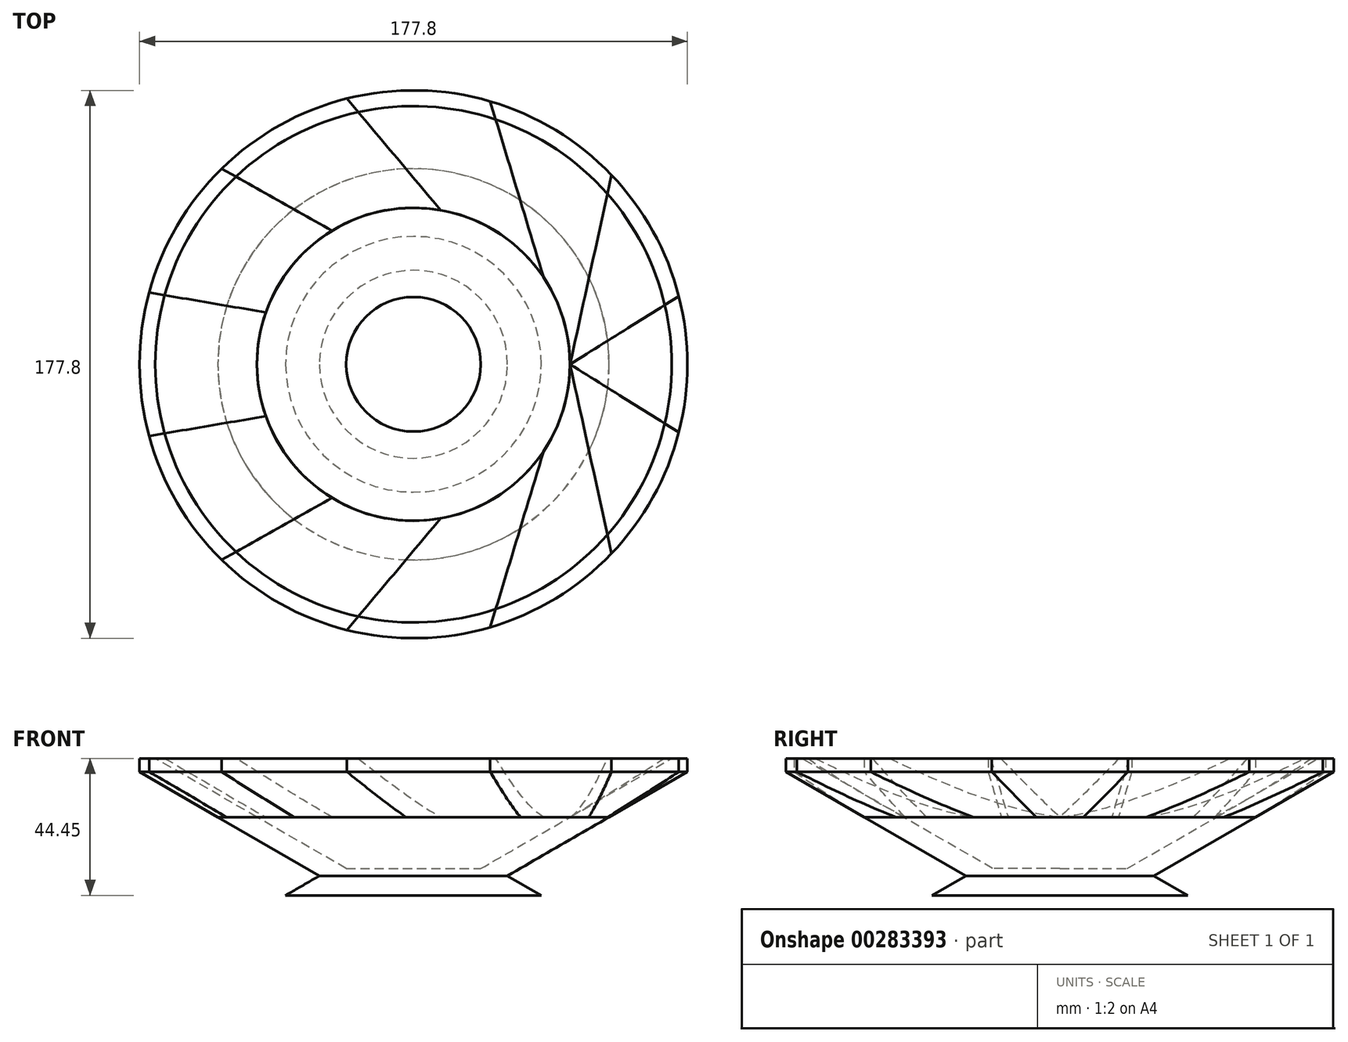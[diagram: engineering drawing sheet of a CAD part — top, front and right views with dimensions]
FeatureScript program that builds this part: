
annotation { "Feature Type Name" : "Feature", "Feature Type Description" : "" }
export const myFeature = defineFeature(function(context is Context, id is Id, definition is map)
    precondition{}
    {
        {
            var Q0;
            Q0=qCreatedBy(makeId("Top.planeOp"),FACE);
            var sketch = newSketch(context, id + "F0", { "sketchPlane" : qUnion([Q0])});
            skCircle(sketch, "E0", {"center": v(0, 0) * mm, "radius": 63.5 * mm});
            skLineSegment(sketch, "E1", {"start": v(0, 0) * mm, "end": v(88.9, 0) * mm, "construction": true});
            skCircle(sketch, "E2.cCircle", {"center": v(0, 0) * mm, "radius": 88.9 * mm});
            skLineSegment(sketch, "E2.0", {"start": v(88.9, 23.82) * mm, "end": v(88.9, -23.82) * mm});
            skLineSegment(sketch, "E2.1", {"start": v(88.9, -23.82) * mm, "end": v(65.08, -65.08) * mm});
            skLineSegment(sketch, "E2.2", {"start": v(65.08, -65.08) * mm, "end": v(23.82, -88.9) * mm});
            skLineSegment(sketch, "E2.3", {"start": v(23.82, -88.9) * mm, "end": v(-23.82, -88.9) * mm});
            skLineSegment(sketch, "E2.4", {"start": v(-23.82, -88.9) * mm, "end": v(-65.08, -65.08) * mm});
            skLineSegment(sketch, "E2.5", {"start": v(-65.08, -65.08) * mm, "end": v(-88.9, -23.82) * mm});
            skLineSegment(sketch, "E2.6", {"start": v(-88.9, -23.82) * mm, "end": v(-88.9, 23.82) * mm});
            skLineSegment(sketch, "E2.7", {"start": v(-88.9, 23.82) * mm, "end": v(-65.08, 65.08) * mm});
            skLineSegment(sketch, "E2.8", {"start": v(-65.08, 65.08) * mm, "end": v(-23.82, 88.9) * mm});
            skLineSegment(sketch, "E2.9", {"start": v(-23.82, 88.9) * mm, "end": v(23.82, 88.9) * mm});
            skLineSegment(sketch, "E2.10", {"start": v(23.82, 88.9) * mm, "end": v(65.08, 65.08) * mm});
            skLineSegment(sketch, "E2.11", {"start": v(65.08, 65.08) * mm, "end": v(88.9, 23.82) * mm});
            skPoint(sketch, "E2.0.midPoint", {"position": v(88.9, 0) * mm});
            skCircle(sketch, "E3", {"center": v(0, 0) * mm, "radius": 50.8 * mm});
            skLineSegment(sketch, "E4", {"start": v(50.8, 0) * mm, "end": v(-65.08, 65.08) * mm, "construction": true});
            skLineSegment(sketch, "E5", {"start": v(50.8, 0) * mm, "end": v(-23.82, 88.9) * mm, "construction": true});
            skLineSegment(sketch, "E6", {"start": v(50.8, 0) * mm, "end": v(23.82, 88.9) * mm, "construction": true});
            skLineSegment(sketch, "E7", {"start": v(50.8, 0) * mm, "end": v(65.08, 65.08) * mm, "construction": true});
            skLineSegment(sketch, "E8", {"start": v(50.8, 0) * mm, "end": v(88.9, 23.82) * mm, "construction": true});
            skLineSegment(sketch, "E9", {"start": v(50.8, 0) * mm, "end": v(88.9, -23.82) * mm, "construction": true});
            skLineSegment(sketch, "E10", {"start": v(50.8, 0) * mm, "end": v(65.08, -65.08) * mm, "construction": true});
            skLineSegment(sketch, "E11", {"start": v(50.8, 0) * mm, "end": v(23.82, -88.9) * mm, "construction": true});
            skLineSegment(sketch, "E12", {"start": v(50.8, 0) * mm, "end": v(-23.82, -88.9) * mm, "construction": true});
            skLineSegment(sketch, "E13", {"start": v(50.8, 0) * mm, "end": v(-65.08, -65.08) * mm, "construction": true});
            skLineSegment(sketch, "E14", {"start": v(-88.9, -23.82) * mm, "end": v(50.8, 0) * mm, "construction": true});
            skLineSegment(sketch, "E15", {"start": v(-88.9, 23.82) * mm, "end": v(50.8, 0) * mm, "construction": true});
            skLineSegment(sketch, "E16", {"start": v(-26.44, -43.38) * mm, "end": v(-65.08, -65.08) * mm});
            skLineSegment(sketch, "E17", {"start": v(-26.44, -43.38) * mm, "end": v(-47.93, -16.83) * mm});
            skLineSegment(sketch, "E18", {"start": v(-88.9, -23.82) * mm, "end": v(-47.93, -16.83) * mm});
            skLineSegment(sketch, "E19", {"start": v(-47.93, -16.83) * mm, "end": v(-47.93, 16.83) * mm});
            skLineSegment(sketch, "E20", {"start": v(-88.9, 23.82) * mm, "end": v(-47.93, 16.83) * mm});
            skLineSegment(sketch, "E21", {"start": v(-26.44, 43.38) * mm, "end": v(-47.93, 16.83) * mm});
            skLineSegment(sketch, "E22", {"start": v(-26.44, 43.38) * mm, "end": v(-65.08, 65.08) * mm});
            skLineSegment(sketch, "E23", {"start": v(-26.44, 43.38) * mm, "end": v(8.8, 50.03) * mm});
            skLineSegment(sketch, "E24", {"start": v(-23.82, 88.9) * mm, "end": v(8.8, 50.03) * mm});
            skLineSegment(sketch, "E25", {"start": v(42.23, 28.23) * mm, "end": v(8.8, 50.03) * mm});
            skLineSegment(sketch, "E26", {"start": v(42.23, 28.23) * mm, "end": v(23.82, 88.9) * mm});
            skLineSegment(sketch, "E27", {"start": v(42.23, 28.23) * mm, "end": v(50.8, 0) * mm});
            skLineSegment(sketch, "E28", {"start": v(50.8, 0) * mm, "end": v(65.08, 65.08) * mm});
            skLineSegment(sketch, "E29", {"start": v(88.9, 23.82) * mm, "end": v(50.8, 0) * mm});
            skLineSegment(sketch, "E30", {"start": v(88.9, -23.82) * mm, "end": v(50.8, 0) * mm});
            skLineSegment(sketch, "E31", {"start": v(65.08, -65.08) * mm, "end": v(50.8, 0) * mm});
            skLineSegment(sketch, "E32", {"start": v(23.82, -88.9) * mm, "end": v(50.8, 0) * mm});
            skLineSegment(sketch, "E33", {"start": v(-23.82, -88.9) * mm, "end": v(8.8, -50.03) * mm});
            skLineSegment(sketch, "E34", {"start": v(8.8, -50.03) * mm, "end": v(-26.44, -43.38) * mm});
            skLineSegment(sketch, "E35", {"start": v(8.8, -50.03) * mm, "end": v(42.23, -28.23) * mm});
            skSolve(sketch);
        }
        {
            var Q0;
            Q0=makeQuery(id+"F0.imprint","IMPRINT",FACE,{"disambiguationData":[TD([[makeQuery(id+"F0.imprint","IMPRINT",EDGE,{"derivedFrom":sQuery(id+"F0.wireOp",EDGE,"E17")}),-1.0]])]});
            var Q1;
            {var subQ0=sQuery(id+"F0.wireOp",EDGE,"E35");Q1=makeQuery(id+"F0.imprint","IMPRINT",FACE,{"disambiguationData":[TD([[makeQuery(id+"F0.imprint","IMPRINT",EDGE,{"derivedFrom":subQ0}),-1.0]])]});}
            var Q2;
            {var subQ0=sQuery(id+"F0.wireOp",EDGE,"E34");Q2=makeQuery(id+"F0.imprint","IMPRINT",FACE,{"disambiguationData":[TD([[makeQuery(id+"F0.imprint","IMPRINT",EDGE,{"derivedFrom":subQ0}),1.0]])]});}
            var Q3;
            {var subQ0=sQuery(id+"F0.wireOp",EDGE,"E17");Q3=makeQuery(id+"F0.imprint","IMPRINT",FACE,{"disambiguationData":[TD([[makeQuery(id+"F0.imprint","IMPRINT",EDGE,{"derivedFrom":subQ0}),1.0]])]});}
            var Q4;
            {var subQ0=sQuery(id+"F0.wireOp",EDGE,"E19");Q4=makeQuery(id+"F0.imprint","IMPRINT",FACE,{"disambiguationData":[TD([[makeQuery(id+"F0.imprint","IMPRINT",EDGE,{"derivedFrom":subQ0}),1.0]])]});}
            var Q5;
            {var subQ0=sQuery(id+"F0.wireOp",EDGE,"E21");Q5=makeQuery(id+"F0.imprint","IMPRINT",FACE,{"disambiguationData":[TD([[makeQuery(id+"F0.imprint","IMPRINT",EDGE,{"derivedFrom":subQ0}),-1.0]])]});}
            var Q6;
            {var subQ0=sQuery(id+"F0.wireOp",EDGE,"E23");Q6=makeQuery(id+"F0.imprint","IMPRINT",FACE,{"disambiguationData":[TD([[makeQuery(id+"F0.imprint","IMPRINT",EDGE,{"derivedFrom":subQ0}),1.0]])]});}
            var Q7;
            {var subQ0=sQuery(id+"F0.wireOp",EDGE,"E24");var subQ1=sQuery(id+"F0.wireOp",EDGE,"E0");var subQ2=makeQuery(id+"F0.imprint","INTERSECT",VERTEX,{"derivedFrom":[subQ1,subQ0]});Q7=makeQuery(id+"F0.imprint","IMPRINT",FACE,{"disambiguationData":[TD([[makeQuery(id+"F0.imprint","IMPRINT",EDGE,{"disambiguationData":[TD([[subQ2,-1.0]])],"derivedFrom":subQ1}),1.0]])]});}
            var Q8;
            {var subQ0=sQuery(id+"F0.wireOp",EDGE,"E22");var subQ1=sQuery(id+"F0.wireOp",EDGE,"E0");var subQ2=makeQuery(id+"F0.imprint","INTERSECT",VERTEX,{"derivedFrom":[subQ1,subQ0]});Q8=makeQuery(id+"F0.imprint","IMPRINT",FACE,{"disambiguationData":[TD([[makeQuery(id+"F0.imprint","IMPRINT",EDGE,{"disambiguationData":[TD([[subQ2,-1.0]])],"derivedFrom":subQ1}),1.0]])]});}
            var Q9;
            {var subQ0=sQuery(id+"F0.wireOp",EDGE,"E20");var subQ1=sQuery(id+"F0.wireOp",EDGE,"E0");var subQ2=makeQuery(id+"F0.imprint","INTERSECT",VERTEX,{"derivedFrom":[subQ1,subQ0]});Q9=makeQuery(id+"F0.imprint","IMPRINT",FACE,{"disambiguationData":[TD([[makeQuery(id+"F0.imprint","IMPRINT",EDGE,{"disambiguationData":[TD([[subQ2,-1.0]])],"derivedFrom":subQ1}),1.0]])]});}
            var Q10;
            {var subQ0=sQuery(id+"F0.wireOp",EDGE,"E18");var subQ1=sQuery(id+"F0.wireOp",EDGE,"E0");var subQ2=makeQuery(id+"F0.imprint","INTERSECT",VERTEX,{"derivedFrom":[subQ1,subQ0]});Q10=makeQuery(id+"F0.imprint","IMPRINT",FACE,{"disambiguationData":[TD([[makeQuery(id+"F0.imprint","IMPRINT",EDGE,{"disambiguationData":[TD([[subQ2,-1.0]])],"derivedFrom":subQ1}),1.0]])]});}
            var Q11;
            {var subQ0=sQuery(id+"F0.wireOp",EDGE,"E16");var subQ1=sQuery(id+"F0.wireOp",EDGE,"E0");var subQ2=makeQuery(id+"F0.imprint","INTERSECT",VERTEX,{"derivedFrom":[subQ1,subQ0]});Q11=makeQuery(id+"F0.imprint","IMPRINT",FACE,{"disambiguationData":[TD([[makeQuery(id+"F0.imprint","IMPRINT",EDGE,{"disambiguationData":[TD([[subQ2,-1.0]])],"derivedFrom":subQ1}),1.0]])]});}
            var Q12;
            {var subQ0=sQuery(id+"F0.wireOp",EDGE,"E33");var subQ1=sQuery(id+"F0.wireOp",EDGE,"E0");var subQ2=makeQuery(id+"F0.imprint","INTERSECT",VERTEX,{"derivedFrom":[subQ1,subQ0]});Q12=makeQuery(id+"F0.imprint","IMPRINT",FACE,{"disambiguationData":[TD([[makeQuery(id+"F0.imprint","IMPRINT",EDGE,{"disambiguationData":[TD([[subQ2,-1.0]])],"derivedFrom":subQ1}),1.0]])]});}
            var Q13;
            {var subQ0=sQuery(id+"F0.wireOp",EDGE,"E31");var subQ1=sQuery(id+"F0.wireOp",EDGE,"E0");var subQ2=makeQuery(id+"F0.imprint","INTERSECT",VERTEX,{"derivedFrom":[subQ1,subQ0]});Q13=makeQuery(id+"F0.imprint","IMPRINT",FACE,{"disambiguationData":[TD([[makeQuery(id+"F0.imprint","IMPRINT",EDGE,{"disambiguationData":[TD([[subQ2,-1.0]])],"derivedFrom":subQ1}),1.0]])]});}
            var Q14;
            {var subQ0=sQuery(id+"F0.wireOp",EDGE,"E29");var subQ1=sQuery(id+"F0.wireOp",EDGE,"E0");var subQ2=makeQuery(id+"F0.imprint","INTERSECT",VERTEX,{"derivedFrom":[subQ1,subQ0]});Q14=makeQuery(id+"F0.imprint","IMPRINT",FACE,{"disambiguationData":[TD([[makeQuery(id+"F0.imprint","IMPRINT",EDGE,{"disambiguationData":[TD([[subQ2,1.0]])],"derivedFrom":subQ1}),1.0]])]});}
            var Q15;
            {var subQ0=sQuery(id+"F0.wireOp",EDGE,"E32");var subQ1=sQuery(id+"F0.wireOp",EDGE,"E3");var subQ3=makeQuery(id+"F0.imprint","INTERSECT",VERTEX,{"derivedFrom":[subQ1,subQ0,sQuery(id+"F0.wireOp",EDGE,"E35")]});Q15=makeQuery(id+"F0.imprint","IMPRINT",FACE,{"disambiguationData":[TD([[makeQuery(id+"F0.imprint","IMPRINT",EDGE,{"disambiguationData":[TD([[subQ3,-1.0]])],"derivedFrom":subQ1}),1.0]])]});}
            var Q16;
            {var subQ0=sQuery(id+"F0.wireOp",EDGE,"E32");var subQ1=sQuery(id+"F0.wireOp",EDGE,"E0");var subQ2=makeQuery(id+"F0.imprint","INTERSECT",VERTEX,{"derivedFrom":[subQ1,subQ0]});Q16=makeQuery(id+"F0.imprint","IMPRINT",FACE,{"disambiguationData":[TD([[makeQuery(id+"F0.imprint","IMPRINT",EDGE,{"disambiguationData":[TD([[subQ2,-1.0]])],"derivedFrom":subQ1}),1.0]])]});}
            var Q17;
            {var subQ0=sQuery(id+"F0.wireOp",EDGE,"E28");var subQ1=sQuery(id+"F0.wireOp",EDGE,"E0");var subQ2=makeQuery(id+"F0.imprint","INTERSECT",VERTEX,{"derivedFrom":[subQ1,subQ0]});Q17=makeQuery(id+"F0.imprint","IMPRINT",FACE,{"disambiguationData":[TD([[makeQuery(id+"F0.imprint","IMPRINT",EDGE,{"disambiguationData":[TD([[subQ2,1.0]])],"derivedFrom":subQ1}),1.0]])]});}
            var Q18;
            {var subQ0=sQuery(id+"F0.wireOp",EDGE,"E28");var subQ1=sQuery(id+"F0.wireOp",EDGE,"E0");var subQ2=makeQuery(id+"F0.imprint","INTERSECT",VERTEX,{"derivedFrom":[subQ1,subQ0]});Q18=makeQuery(id+"F0.imprint","IMPRINT",FACE,{"disambiguationData":[TD([[makeQuery(id+"F0.imprint","IMPRINT",EDGE,{"disambiguationData":[TD([[subQ2,-1.0]])],"derivedFrom":subQ1}),1.0]])]});}
            var Q19;
            {var subQ0=sQuery(id+"F0.wireOp",EDGE,"E26");var subQ1=sQuery(id+"F0.wireOp",EDGE,"E0");var subQ2=makeQuery(id+"F0.imprint","INTERSECT",VERTEX,{"derivedFrom":[subQ1,subQ0]});Q19=makeQuery(id+"F0.imprint","IMPRINT",FACE,{"disambiguationData":[TD([[makeQuery(id+"F0.imprint","IMPRINT",EDGE,{"disambiguationData":[TD([[subQ2,-1.0]])],"derivedFrom":subQ1}),1.0]])]});}
            var Q20;
            {var subQ0=sQuery(id+"F0.wireOp",EDGE,"E25");Q20=makeQuery(id+"F0.imprint","IMPRINT",FACE,{"disambiguationData":[TD([[makeQuery(id+"F0.imprint","IMPRINT",EDGE,{"derivedFrom":subQ0}),-1.0]])]});}
            var Q21;
            {var subQ0=sQuery(id+"F0.wireOp",EDGE,"E27");Q21=makeQuery(id+"F0.imprint","IMPRINT",FACE,{"disambiguationData":[TD([[makeQuery(id+"F0.imprint","IMPRINT",EDGE,{"derivedFrom":subQ0}),1.0]])]});}
            extrude(context, id + "F1", {"entities" : qUnion([Q0, Q1, Q2, Q3, Q4, Q5, Q6, Q7, Q8, Q9, Q10, Q11, Q12, Q13, Q14, Q15, Q16, Q17, Q18, Q19, Q20, Q21]), "oppositeDirection" : true, "depth" : 25.4 * mm, "offsetDistance" : 25.4 * mm});
        }
        {
            var Q0;
            {var subQ1=sQuery(id+"F0.wireOp",EDGE,"E0");var subQ6=sQuery(id+"F0.wireOp",EDGE,"E32");var subQ8=makeQuery(id+"F0.imprint","INTERSECT",VERTEX,{"derivedFrom":[subQ1,subQ6]});Q0=makeQuery(id+"F0.imprint","IMPRINT",FACE,{"disambiguationData":[TD([[makeQuery(id+"F0.imprint","IMPRINT",EDGE,{"disambiguationData":[TD([[subQ8,-1.0]])],"derivedFrom":subQ1}),-1.0]])]});}
            var Q1;
            {var subQ0=sQuery(id+"F0.wireOp",EDGE,"E32");var subQ1=sQuery(id+"F0.wireOp",EDGE,"E0");var subQ2=makeQuery(id+"F0.imprint","INTERSECT",VERTEX,{"derivedFrom":[subQ1,subQ0]});Q1=makeQuery(id+"F0.imprint","IMPRINT",FACE,{"disambiguationData":[TD([[makeQuery(id+"F0.imprint","IMPRINT",EDGE,{"disambiguationData":[TD([[subQ2,-1.0]])],"derivedFrom":subQ1}),1.0]])]});}
            var Q2;
            {var subQ0=sQuery(id+"F0.wireOp",EDGE,"E16");var subQ1=sQuery(id+"F0.wireOp",EDGE,"E0");var subQ2=makeQuery(id+"F0.imprint","INTERSECT",VERTEX,{"derivedFrom":[subQ1,subQ0]});Q2=makeQuery(id+"F0.imprint","IMPRINT",FACE,{"disambiguationData":[TD([[makeQuery(id+"F0.imprint","IMPRINT",EDGE,{"disambiguationData":[TD([[subQ2,-1.0]])],"derivedFrom":subQ1}),1.0]])]});}
            var Q3;
            {var subQ0=sQuery(id+"F0.wireOp",EDGE,"E16");var subQ1=sQuery(id+"F0.wireOp",EDGE,"E0");var subQ2=makeQuery(id+"F0.imprint","INTERSECT",VERTEX,{"derivedFrom":[subQ1,subQ0]});Q3=makeQuery(id+"F0.imprint","IMPRINT",FACE,{"disambiguationData":[TD([[makeQuery(id+"F0.imprint","IMPRINT",EDGE,{"disambiguationData":[TD([[subQ2,-1.0]])],"derivedFrom":subQ1}),-1.0]])]});}
            var Q4;
            {var subQ0=sQuery(id+"F0.wireOp",EDGE,"E20");var subQ1=sQuery(id+"F0.wireOp",EDGE,"E0");var subQ2=makeQuery(id+"F0.imprint","INTERSECT",VERTEX,{"derivedFrom":[subQ1,subQ0]});Q4=makeQuery(id+"F0.imprint","IMPRINT",FACE,{"disambiguationData":[TD([[makeQuery(id+"F0.imprint","IMPRINT",EDGE,{"disambiguationData":[TD([[subQ2,-1.0]])],"derivedFrom":subQ1}),1.0]])]});}
            var Q5;
            {var subQ1=sQuery(id+"F0.wireOp",EDGE,"E0");var subQ6=sQuery(id+"F0.wireOp",EDGE,"E20");var subQ8=makeQuery(id+"F0.imprint","INTERSECT",VERTEX,{"derivedFrom":[subQ1,subQ6]});Q5=makeQuery(id+"F0.imprint","IMPRINT",FACE,{"disambiguationData":[TD([[makeQuery(id+"F0.imprint","IMPRINT",EDGE,{"disambiguationData":[TD([[subQ8,-1.0]])],"derivedFrom":subQ1}),-1.0]])]});}
            var Q6;
            {var subQ0=sQuery(id+"F0.wireOp",EDGE,"E24");var subQ1=sQuery(id+"F0.wireOp",EDGE,"E0");var subQ2=makeQuery(id+"F0.imprint","INTERSECT",VERTEX,{"derivedFrom":[subQ1,subQ0]});Q6=makeQuery(id+"F0.imprint","IMPRINT",FACE,{"disambiguationData":[TD([[makeQuery(id+"F0.imprint","IMPRINT",EDGE,{"disambiguationData":[TD([[subQ2,-1.0]])],"derivedFrom":subQ1}),1.0]])]});}
            var Q7;
            {var subQ1=sQuery(id+"F0.wireOp",EDGE,"E0");var subQ6=sQuery(id+"F0.wireOp",EDGE,"E24");var subQ7=makeQuery(id+"F0.imprint","INTERSECT",VERTEX,{"derivedFrom":[subQ1,subQ6]});Q7=makeQuery(id+"F0.imprint","IMPRINT",FACE,{"disambiguationData":[TD([[makeQuery(id+"F0.imprint","IMPRINT",EDGE,{"disambiguationData":[TD([[subQ7,-1.0]])],"derivedFrom":subQ1}),-1.0]])]});}
            var Q8;
            {var subQ0=sQuery(id+"F0.wireOp",EDGE,"E28");var subQ1=sQuery(id+"F0.wireOp",EDGE,"E0");var subQ2=makeQuery(id+"F0.imprint","INTERSECT",VERTEX,{"derivedFrom":[subQ1,subQ0]});Q8=makeQuery(id+"F0.imprint","IMPRINT",FACE,{"disambiguationData":[TD([[makeQuery(id+"F0.imprint","IMPRINT",EDGE,{"disambiguationData":[TD([[subQ2,-1.0]])],"derivedFrom":subQ1}),1.0]])]});}
            var Q9;
            {var subQ1=sQuery(id+"F0.wireOp",EDGE,"E0");var subQ6=sQuery(id+"F0.wireOp",EDGE,"E28");var subQ8=makeQuery(id+"F0.imprint","INTERSECT",VERTEX,{"derivedFrom":[subQ1,subQ6]});Q9=makeQuery(id+"F0.imprint","IMPRINT",FACE,{"disambiguationData":[TD([[makeQuery(id+"F0.imprint","IMPRINT",EDGE,{"disambiguationData":[TD([[subQ8,-1.0]])],"derivedFrom":subQ1}),-1.0]])]});}
            var Q10;
            {var subQ4=sQuery(id+"F0.wireOp",EDGE,"E29");var subQ5=sQuery(id+"F0.wireOp",EDGE,"E0");var subQ6=makeQuery(id+"F0.imprint","INTERSECT",VERTEX,{"derivedFrom":[subQ5,subQ4]});Q10=makeQuery(id+"F0.imprint","IMPRINT",FACE,{"disambiguationData":[TD([[makeQuery(id+"F0.imprint","IMPRINT",EDGE,{"disambiguationData":[TD([[subQ6,1.0]])],"derivedFrom":subQ5}),-1.0]])]});}
            var Q11;
            {var subQ0=sQuery(id+"F0.wireOp",EDGE,"E29");var subQ1=sQuery(id+"F0.wireOp",EDGE,"E0");var subQ2=makeQuery(id+"F0.imprint","INTERSECT",VERTEX,{"derivedFrom":[subQ1,subQ0]});Q11=makeQuery(id+"F0.imprint","IMPRINT",FACE,{"disambiguationData":[TD([[makeQuery(id+"F0.imprint","IMPRINT",EDGE,{"disambiguationData":[TD([[subQ2,1.0]])],"derivedFrom":subQ1}),1.0]])]});}
            extrude(context, id + "F2", {"entities" : qUnion([Q0, Q1, Q2, Q3, Q4, Q5, Q6, Q7, Q8, Q9, Q10, Q11]), "depth" : 19.05 * mm, "offsetDistance" : 25.4 * mm});
        }
        {
            var Q0;
            {var subQ1=sQuery(id+"F0.wireOp",EDGE,"E0");var subQ6=sQuery(id+"F0.wireOp",EDGE,"E33");var subQ8=makeQuery(id+"F0.imprint","INTERSECT",VERTEX,{"derivedFrom":[subQ1,subQ6]});Q0=makeQuery(id+"F0.imprint","IMPRINT",FACE,{"disambiguationData":[TD([[makeQuery(id+"F0.imprint","IMPRINT",EDGE,{"disambiguationData":[TD([[subQ8,-1.0]])],"derivedFrom":subQ1}),-1.0]])]});}
            var Q1;
            {var subQ0=sQuery(id+"F0.wireOp",EDGE,"E33");var subQ1=sQuery(id+"F0.wireOp",EDGE,"E0");var subQ2=makeQuery(id+"F0.imprint","INTERSECT",VERTEX,{"derivedFrom":[subQ1,subQ0]});Q1=makeQuery(id+"F0.imprint","IMPRINT",FACE,{"disambiguationData":[TD([[makeQuery(id+"F0.imprint","IMPRINT",EDGE,{"disambiguationData":[TD([[subQ2,-1.0]])],"derivedFrom":subQ1}),1.0]])]});}
            var Q2;
            {var subQ1=sQuery(id+"F0.wireOp",EDGE,"E0");var subQ6=sQuery(id+"F0.wireOp",EDGE,"E18");var subQ8=makeQuery(id+"F0.imprint","INTERSECT",VERTEX,{"derivedFrom":[subQ1,subQ6]});Q2=makeQuery(id+"F0.imprint","IMPRINT",FACE,{"disambiguationData":[TD([[makeQuery(id+"F0.imprint","IMPRINT",EDGE,{"disambiguationData":[TD([[subQ8,-1.0]])],"derivedFrom":subQ1}),-1.0]])]});}
            var Q3;
            {var subQ0=sQuery(id+"F0.wireOp",EDGE,"E18");var subQ1=sQuery(id+"F0.wireOp",EDGE,"E0");var subQ2=makeQuery(id+"F0.imprint","INTERSECT",VERTEX,{"derivedFrom":[subQ1,subQ0]});Q3=makeQuery(id+"F0.imprint","IMPRINT",FACE,{"disambiguationData":[TD([[makeQuery(id+"F0.imprint","IMPRINT",EDGE,{"disambiguationData":[TD([[subQ2,-1.0]])],"derivedFrom":subQ1}),1.0]])]});}
            var Q4;
            {var subQ1=sQuery(id+"F0.wireOp",EDGE,"E0");var subQ6=sQuery(id+"F0.wireOp",EDGE,"E22");var subQ8=makeQuery(id+"F0.imprint","INTERSECT",VERTEX,{"derivedFrom":[subQ1,subQ6]});Q4=makeQuery(id+"F0.imprint","IMPRINT",FACE,{"disambiguationData":[TD([[makeQuery(id+"F0.imprint","IMPRINT",EDGE,{"disambiguationData":[TD([[subQ8,-1.0]])],"derivedFrom":subQ1}),-1.0]])]});}
            var Q5;
            {var subQ0=sQuery(id+"F0.wireOp",EDGE,"E22");var subQ1=sQuery(id+"F0.wireOp",EDGE,"E0");var subQ2=makeQuery(id+"F0.imprint","INTERSECT",VERTEX,{"derivedFrom":[subQ1,subQ0]});Q5=makeQuery(id+"F0.imprint","IMPRINT",FACE,{"disambiguationData":[TD([[makeQuery(id+"F0.imprint","IMPRINT",EDGE,{"disambiguationData":[TD([[subQ2,-1.0]])],"derivedFrom":subQ1}),1.0]])]});}
            var Q6;
            {var subQ1=sQuery(id+"F0.wireOp",EDGE,"E0");var subQ6=sQuery(id+"F0.wireOp",EDGE,"E26");var subQ8=makeQuery(id+"F0.imprint","INTERSECT",VERTEX,{"derivedFrom":[subQ1,subQ6]});Q6=makeQuery(id+"F0.imprint","IMPRINT",FACE,{"disambiguationData":[TD([[makeQuery(id+"F0.imprint","IMPRINT",EDGE,{"disambiguationData":[TD([[subQ8,-1.0]])],"derivedFrom":subQ1}),-1.0]])]});}
            var Q7;
            {var subQ0=sQuery(id+"F0.wireOp",EDGE,"E26");var subQ1=sQuery(id+"F0.wireOp",EDGE,"E0");var subQ2=makeQuery(id+"F0.imprint","INTERSECT",VERTEX,{"derivedFrom":[subQ1,subQ0]});Q7=makeQuery(id+"F0.imprint","IMPRINT",FACE,{"disambiguationData":[TD([[makeQuery(id+"F0.imprint","IMPRINT",EDGE,{"disambiguationData":[TD([[subQ2,-1.0]])],"derivedFrom":subQ1}),1.0]])]});}
            var Q8;
            {var subQ0=sQuery(id+"F0.wireOp",EDGE,"E28");var subQ1=sQuery(id+"F0.wireOp",EDGE,"E0");var subQ2=makeQuery(id+"F0.imprint","INTERSECT",VERTEX,{"derivedFrom":[subQ1,subQ0]});Q8=makeQuery(id+"F0.imprint","IMPRINT",FACE,{"disambiguationData":[TD([[makeQuery(id+"F0.imprint","IMPRINT",EDGE,{"disambiguationData":[TD([[subQ2,1.0]])],"derivedFrom":subQ1}),-1.0]])]});}
            var Q9;
            {var subQ0=sQuery(id+"F0.wireOp",EDGE,"E28");var subQ1=sQuery(id+"F0.wireOp",EDGE,"E0");var subQ2=makeQuery(id+"F0.imprint","INTERSECT",VERTEX,{"derivedFrom":[subQ1,subQ0]});Q9=makeQuery(id+"F0.imprint","IMPRINT",FACE,{"disambiguationData":[TD([[makeQuery(id+"F0.imprint","IMPRINT",EDGE,{"disambiguationData":[TD([[subQ2,1.0]])],"derivedFrom":subQ1}),1.0]])]});}
            var Q10;
            {var subQ4=sQuery(id+"F0.wireOp",EDGE,"E0");var subQ6=sQuery(id+"F0.wireOp",EDGE,"E31");var subQ8=makeQuery(id+"F0.imprint","INTERSECT",VERTEX,{"derivedFrom":[subQ4,subQ6]});Q10=makeQuery(id+"F0.imprint","IMPRINT",FACE,{"disambiguationData":[TD([[makeQuery(id+"F0.imprint","IMPRINT",EDGE,{"disambiguationData":[TD([[subQ8,-1.0]])],"derivedFrom":subQ4}),-1.0]])]});}
            var Q11;
            {var subQ0=sQuery(id+"F0.wireOp",EDGE,"E31");var subQ1=sQuery(id+"F0.wireOp",EDGE,"E0");var subQ2=makeQuery(id+"F0.imprint","INTERSECT",VERTEX,{"derivedFrom":[subQ1,subQ0]});Q11=makeQuery(id+"F0.imprint","IMPRINT",FACE,{"disambiguationData":[TD([[makeQuery(id+"F0.imprint","IMPRINT",EDGE,{"disambiguationData":[TD([[subQ2,-1.0]])],"derivedFrom":subQ1}),1.0]])]});}
            extrude(context, id + "F3", {"entities" : qUnion([Q0, Q1, Q2, Q3, Q4, Q5, Q6, Q7, Q8, Q9, Q10, Q11]), "depth" : 19.05 * mm, "offsetDistance" : 25.4 * mm});
        }
        {
            var Q0;
            Q0=qCreatedBy(makeId("Right.planeOp"),FACE);
            var sketch = newSketch(context, id + "F4", { "sketchPlane" : qUnion([Q0])});
            skLineSegment(sketch, "E36", {"start": v(0, 0) * mm, "end": v(-63.5, 0) * mm, "construction": true});
            skLineSegment(sketch, "E37", {"start": v(0, 0) * mm, "end": v(0, 127) * mm, "construction": true});
            skLineSegment(sketch, "E38", {"start": v(-63.5, 0) * mm, "end": v(-30.5, -19.05) * mm});
            skLineSegment(sketch, "E39", {"start": v(-30.5, -19.05) * mm, "end": v(-52.5, -31.75) * mm});
            skLineSegment(sketch, "E40", {"start": v(-30.5, -19.05) * mm, "end": v(-96.5, 19.05) * mm});
            skLineSegment(sketch, "E41", {"start": v(-96.5, 19.05) * mm, "end": v(-93.32, 24.55) * mm});
            skLineSegment(sketch, "E42", {"start": v(-93.32, 24.55) * mm, "end": v(-21.83, -16.73) * mm});
            skLineSegment(sketch, "E43", {"start": v(-21.83, -16.73) * mm, "end": v(0, -16.73) * mm});
            skLineSegment(sketch, "E44", {"start": v(0, -16.73) * mm, "end": v(0, 59.47) * mm});
            skLineSegment(sketch, "E45", {"start": v(0, 59.47) * mm, "end": v(-127, 59.47) * mm});
            skLineSegment(sketch, "E46", {"start": v(-127, 59.47) * mm, "end": v(-127, -30.12) * mm});
            skLineSegment(sketch, "E47", {"start": v(-127, -30.12) * mm, "end": v(-52.5, -31.75) * mm});
            skSolve(sketch);
        }
        {
            var Q0;
            Q0 = qSketchRegion(id + "F4", true);
            var Q1;
            Q1=sQuery(id+"F4.wireOp",EDGE,"E37");
            revolve(context, id + "F5", {"surfaceOperationType" : NewSurfaceOperationType.NEW, "entities" : qUnion([Q0]), "axis" : qUnion([Q1]), "revolveType" : RevolveType.FULL});
        }
        {
            var Q0;
            Q0=makeQuery(id+"F5.opRevolve","SWEPT_BODY",BODY,{"disambiguationData":[OSD([sQuery(id+"F4.wireOp",EDGE,"E39"),sQuery(id+"F4.wireOp",EDGE,"E40"),sQuery(id+"F4.wireOp",EDGE,"E41"),sQuery(id+"F4.wireOp",EDGE,"E42"),sQuery(id+"F4.wireOp",EDGE,"E43"),sQuery(id+"F4.wireOp",EDGE,"E44"),sQuery(id+"F4.wireOp",EDGE,"E45"),sQuery(id+"F4.wireOp",EDGE,"E46"),sQuery(id+"F4.wireOp",EDGE,"E47")])]});
            var Q1;
            Q1=makeQuery(id+"F3.opExtrude","SWEPT_BODY",BODY,{"disambiguationData":[OSD([sQuery(id+"F0.wireOp",EDGE,"E2.cCircle"),sQuery(id+"F0.wireOp",EDGE,"E30"),sQuery(id+"F0.wireOp",EDGE,"E31")])]});
            var Q2;
            Q2=makeQuery(id+"F3.opExtrude","SWEPT_BODY",BODY,{"disambiguationData":[OSD([sQuery(id+"F0.wireOp",EDGE,"E2.cCircle"),sQuery(id+"F0.wireOp",EDGE,"E3"),sQuery(id+"F0.wireOp",EDGE,"E16"),sQuery(id+"F0.wireOp",EDGE,"E18")])]});
            var Q3;
            Q3=makeQuery(id+"F3.opExtrude","SWEPT_BODY",BODY,{"disambiguationData":[OSD([sQuery(id+"F0.wireOp",EDGE,"E2.cCircle"),sQuery(id+"F0.wireOp",EDGE,"E3"),sQuery(id+"F0.wireOp",EDGE,"E32"),sQuery(id+"F0.wireOp",EDGE,"E33")])]});
            var Q4;
            Q4=makeQuery(id+"F3.opExtrude","SWEPT_BODY",BODY,{"disambiguationData":[OSD([sQuery(id+"F0.wireOp",EDGE,"E2.cCircle"),sQuery(id+"F0.wireOp",EDGE,"E3"),sQuery(id+"F0.wireOp",EDGE,"E20"),sQuery(id+"F0.wireOp",EDGE,"E22")])]});
            var Q5;
            Q5=makeQuery(id+"F3.opExtrude","SWEPT_BODY",BODY,{"disambiguationData":[OSD([sQuery(id+"F0.wireOp",EDGE,"E2.cCircle"),sQuery(id+"F0.wireOp",EDGE,"E3"),sQuery(id+"F0.wireOp",EDGE,"E24"),sQuery(id+"F0.wireOp",EDGE,"E26")])]});
            var Q6;
            Q6=makeQuery(id+"F3.opExtrude","SWEPT_BODY",BODY,{"disambiguationData":[OSD([sQuery(id+"F0.wireOp",EDGE,"E2.cCircle"),sQuery(id+"F0.wireOp",EDGE,"E28"),sQuery(id+"F0.wireOp",EDGE,"E29")])]});
            var Q7;
            Q7=makeQuery(id+"F2.opExtrude","SWEPT_BODY",BODY,{"disambiguationData":[OSD([sQuery(id+"F0.wireOp",EDGE,"E2.cCircle"),sQuery(id+"F0.wireOp",EDGE,"E3"),sQuery(id+"F0.wireOp",EDGE,"E31"),sQuery(id+"F0.wireOp",EDGE,"E32")])]});
            var Q8;
            Q8=makeQuery(id+"F2.opExtrude","SWEPT_BODY",BODY,{"disambiguationData":[OSD([sQuery(id+"F0.wireOp",EDGE,"E2.cCircle"),sQuery(id+"F0.wireOp",EDGE,"E3"),sQuery(id+"F0.wireOp",EDGE,"E16"),sQuery(id+"F0.wireOp",EDGE,"E33")])]});
            var Q9;
            Q9=makeQuery(id+"F2.opExtrude","SWEPT_BODY",BODY,{"disambiguationData":[OSD([sQuery(id+"F0.wireOp",EDGE,"E2.cCircle"),sQuery(id+"F0.wireOp",EDGE,"E3"),sQuery(id+"F0.wireOp",EDGE,"E18"),sQuery(id+"F0.wireOp",EDGE,"E20")])]});
            var Q10;
            Q10=makeQuery(id+"F2.opExtrude","SWEPT_BODY",BODY,{"disambiguationData":[OSD([sQuery(id+"F0.wireOp",EDGE,"E2.cCircle"),sQuery(id+"F0.wireOp",EDGE,"E3"),sQuery(id+"F0.wireOp",EDGE,"E22"),sQuery(id+"F0.wireOp",EDGE,"E24")])]});
            var Q11;
            Q11=makeQuery(id+"F2.opExtrude","SWEPT_BODY",BODY,{"disambiguationData":[OSD([sQuery(id+"F0.wireOp",EDGE,"E2.cCircle"),sQuery(id+"F0.wireOp",EDGE,"E3"),sQuery(id+"F0.wireOp",EDGE,"E26"),sQuery(id+"F0.wireOp",EDGE,"E28")])]});
            var Q12;
            Q12=makeQuery(id+"F2.opExtrude","SWEPT_BODY",BODY,{"disambiguationData":[OSD([sQuery(id+"F0.wireOp",EDGE,"E2.cCircle"),sQuery(id+"F0.wireOp",EDGE,"E29"),sQuery(id+"F0.wireOp",EDGE,"E30")])]});
            var Q13;
            Q13=makeQuery(id+"F1.opExtrude","SWEPT_BODY",BODY,{"disambiguationData":[OSD([sQuery(id+"F0.wireOp",EDGE,"E0")])]});
            booleanBodies(context, id + "F6", {"operationType" : BooleanOperationType.SUBTRACTION, "tools" : qUnion([Q0]), "targets" : qUnion([Q1, Q2, Q3, Q4, Q5, Q6, Q7, Q8, Q9, Q10, Q11, Q12, Q13])});
        }
    });
